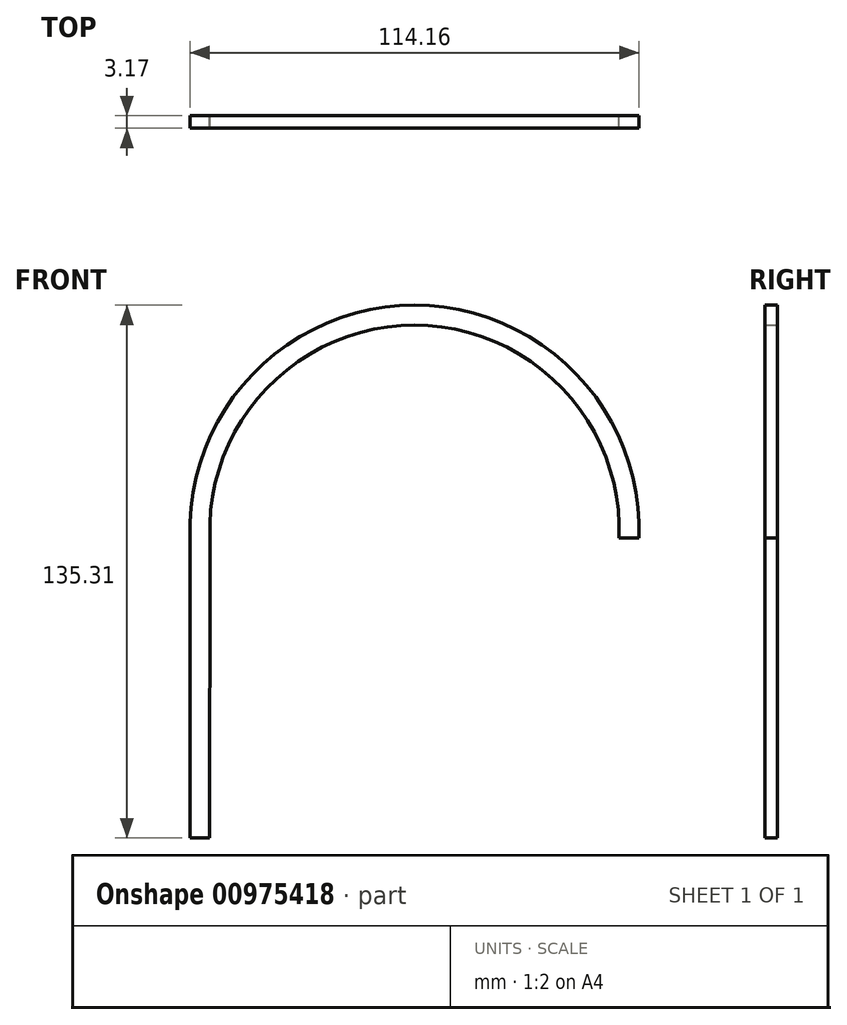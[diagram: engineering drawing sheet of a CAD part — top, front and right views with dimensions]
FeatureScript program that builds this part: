
annotation { "Feature Type Name" : "Feature", "Feature Type Description" : "" }
export const myFeature = defineFeature(function(context is Context, id is Id, definition is map)
    precondition{}
    {
        {
            var Q0;
            Q0=qCreatedBy(makeId("Front.planeOp"),FACE);
            var sketch = newSketch(context, id + "F0", { "sketchPlane" : qUnion([Q0])});
            skArc(sketch, "E0", {"start": v(55.84, 0) * mm, "mid": v(-1.2, 59.11) * mm, "end": v(-58.24, 0) * mm});
            skArc(sketch, "E1", {"start": v(50.76, 0) * mm, "mid": v(-1.2, 54.04) * mm, "end": v(-53.16, 0) * mm});
            skLineSegment(sketch, "E2", {"start": v(-58.24, 0) * mm, "end": v(-58.24, -76.2) * mm});
            skLineSegment(sketch, "E3", {"start": v(-58.24, -76.2) * mm, "end": v(-53.22, -76.2) * mm});
            skLineSegment(sketch, "E4", {"start": v(-53.22, -76.2) * mm, "end": v(-53.16, 0) * mm});
            skLineSegment(sketch, "E5", {"start": v(50.76, 0) * mm, "end": v(55.84, 0) * mm});
            skSolve(sketch);
        }
        {
            var Q0;
            Q0 = qSketchRegion(id + "F0", true);
            extrude(context, id + "F1", {"entities" : qUnion([Q0]), "depth" : 3.17 * mm, "offsetDistance" : 25.4 * mm});
        }
    });
